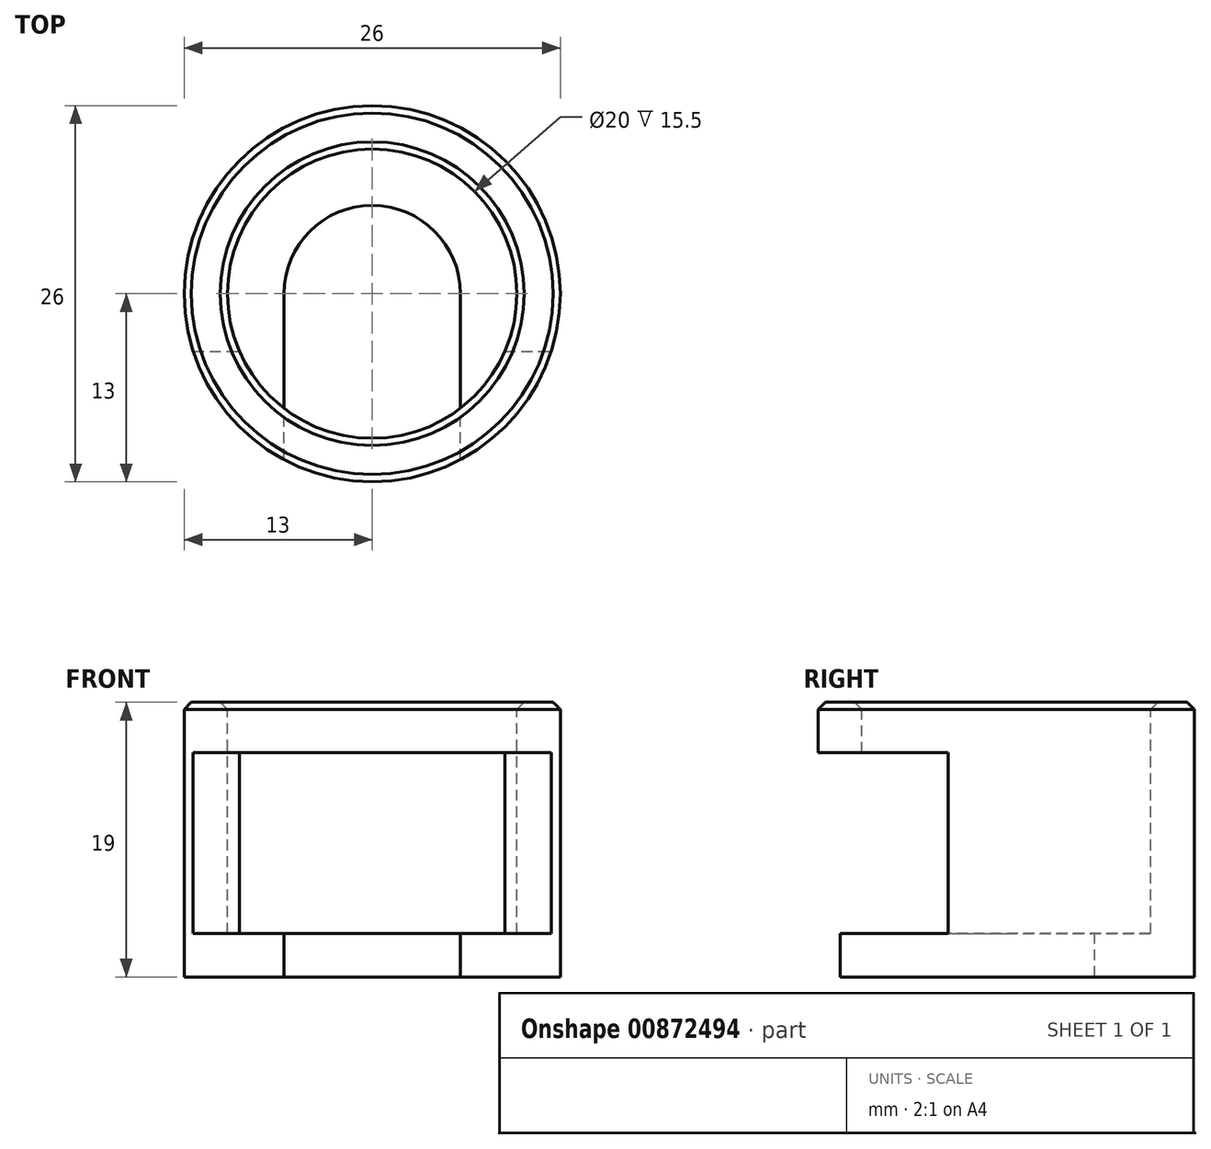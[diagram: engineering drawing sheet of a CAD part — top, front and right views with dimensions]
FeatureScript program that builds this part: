
annotation { "Feature Type Name" : "Feature", "Feature Type Description" : "" }
export const myFeature = defineFeature(function(context is Context, id is Id, definition is map)
    precondition{}
    {
        {
            var Q0;
            Q0=qCreatedBy(makeId("Front.planeOp"),FACE);
            var sketch = newSketch(context, id + "F0", { "sketchPlane" : qUnion([Q0])});
            skLineSegment(sketch, "E0", {"start": v(10, 0) * mm, "end": v(10, 16) * mm});
            skLineSegment(sketch, "E1", {"start": v(10, 16) * mm, "end": v(13, 16) * mm});
            skLineSegment(sketch, "E2", {"start": v(13, 16) * mm, "end": v(13, -3) * mm});
            skLineSegment(sketch, "E3", {"start": v(13, -3) * mm, "end": v(6.1, -3) * mm});
            skLineSegment(sketch, "E4", {"start": v(6.1, 0) * mm, "end": v(10, 0) * mm});
            skLineSegment(sketch, "E5", {"start": v(0, 22.82) * mm, "end": v(0, -9.3) * mm, "construction": true});
            skLineSegment(sketch, "E6", {"start": v(6.1, 0) * mm, "end": v(6.1, -3) * mm});
            skPoint(sketch, "E7.orphan", {"position": v(0, -3) * mm});
            skSolve(sketch);
        }
        {
            var Q0;
            Q0 = qSketchRegion(id + "F0", true);
            var Q1;
            Q1=sQuery(id+"F0.wireOp",EDGE,"E5");
            revolve(context, id + "F1", {"surfaceOperationType" : NewSurfaceOperationType.NEW, "entities" : qUnion([Q0]), "axis" : qUnion([Q1]), "revolveType" : RevolveType.FULL});
        }
        {
            var Q0;
            Q0=makeQuery(id+"F1.opRevolve","SWEPT_EDGE",EDGE,{"disambiguationData":[OSD([sQuery(id+"F0.wireOp",EDGE,"E1"),sQuery(id+"F0.wireOp",EDGE,"E2")])]});
            chamfer(context, id + "F2", {"entities" : qUnion([Q0]), "width" : 0.5 * mm, "tangentPropagation" : true});
        }
        {
            var Q0;
            Q0=makeQuery(id+"F1.opRevolve","SWEPT_EDGE",EDGE,{"disambiguationData":[OSD([sQuery(id+"F0.wireOp",EDGE,"E0"),sQuery(id+"F0.wireOp",EDGE,"E1")])]});
            chamfer(context, id + "F3", {"entities" : qUnion([Q0]), "width" : 0.5 * mm, "tangentPropagation" : true});
        }
        {
            var Q0;
            Q0=qCreatedBy(makeId("Front.planeOp"),FACE);
            var sketch = newSketch(context, id + "F4", { "sketchPlane" : qUnion([Q0])});
            skLineSegment(sketch, "E8", {"start": v(9.1, 0) * mm, "end": v(6.1, 0) * mm});
            skLineSegment(sketch, "E9", {"start": v(6.1, 5) * mm, "end": v(6.1, -5.68) * mm});
            skLineSegment(sketch, "E10", {"start": v(6.1, -5.68) * mm, "end": v(0, -5.68) * mm});
            skLineSegment(sketch, "E11", {"start": v(6.1, 5) * mm, "end": v(0, 5) * mm});
            skLineSegment(sketch, "E12", {"start": v(0, 0) * mm, "end": v(0, 18.82) * mm, "construction": true});
            skLineSegment(sketch, "E13", {"start": v(0, 0) * mm, "end": v(0, -9.84) * mm, "construction": true});
            skLineSegment(sketch, "E14.MirrorCS", {"start": v(-6.1, 5) * mm, "end": v(0, 5) * mm});
            skLineSegment(sketch, "E15.MirrorCS", {"start": v(-6.1, 5) * mm, "end": v(-6.1, -5.68) * mm});
            skLineSegment(sketch, "E16.MirrorCS", {"start": v(-6.1, -5.68) * mm, "end": v(0, -5.68) * mm});
            skPoint(sketch, "E17.orphan", {"position": v(-6.1, 0) * mm});
            skPoint(sketch, "E18.start.orphan", {"position": v(9.1, 5) * mm});
            skPoint(sketch, "E19.orphan", {"position": v(-9.1, 5) * mm});
            skPoint(sketch, "E20.MirrorCS.end.orphan", {"position": v(-9.1, 0) * mm});
            skSolve(sketch);
        }
        {
            var Q0;
            Q0 = qSketchRegion(id + "F4", true);
            extrude(context, id + "F5", {"entities" : qUnion([Q0]), "operationType" : NewBodyOperationType.REMOVE, "oppositeDirection" : true, "depth" : -20 * mm, "offsetDistance" : 25 * mm});
        }
        {
            var Q0;
            Q0=qCreatedBy(makeId("Right.planeOp"),FACE);
            var sketch = newSketch(context, id + "F6", { "sketchPlane" : qUnion([Q0])});
            skLineSegment(sketch, "E21.bottom", {"start": v(-20, 12.5) * mm, "end": v(-4, 12.5) * mm});
            skLineSegment(sketch, "E21.top", {"start": v(-20, 0) * mm, "end": v(-4, 0) * mm});
            skLineSegment(sketch, "E21.left", {"start": v(-20, 12.5) * mm, "end": v(-20, 0) * mm});
            skLineSegment(sketch, "E21.right", {"start": v(-4, 12.5) * mm, "end": v(-4, 0) * mm});
            skSolve(sketch);
        }
        {
            var Q0;
            Q0=makeQuery(id+"F6.imprint","IMPRINT",FACE,{"disambiguationData":[TD([[makeQuery(id+"F6.imprint","IMPRINT",EDGE,{"derivedFrom":sQuery(id+"F6.wireOp",EDGE,"E21.bottom")}),-1.0]])]});
            extrude(context, id + "F7", {"entities" : qUnion([Q0]), "operationType" : NewBodyOperationType.REMOVE, "oppositeDirection" : true, "depth" : 30 * mm, "offsetDistance" : 25 * mm, "symmetric" : true});
        }
    });
